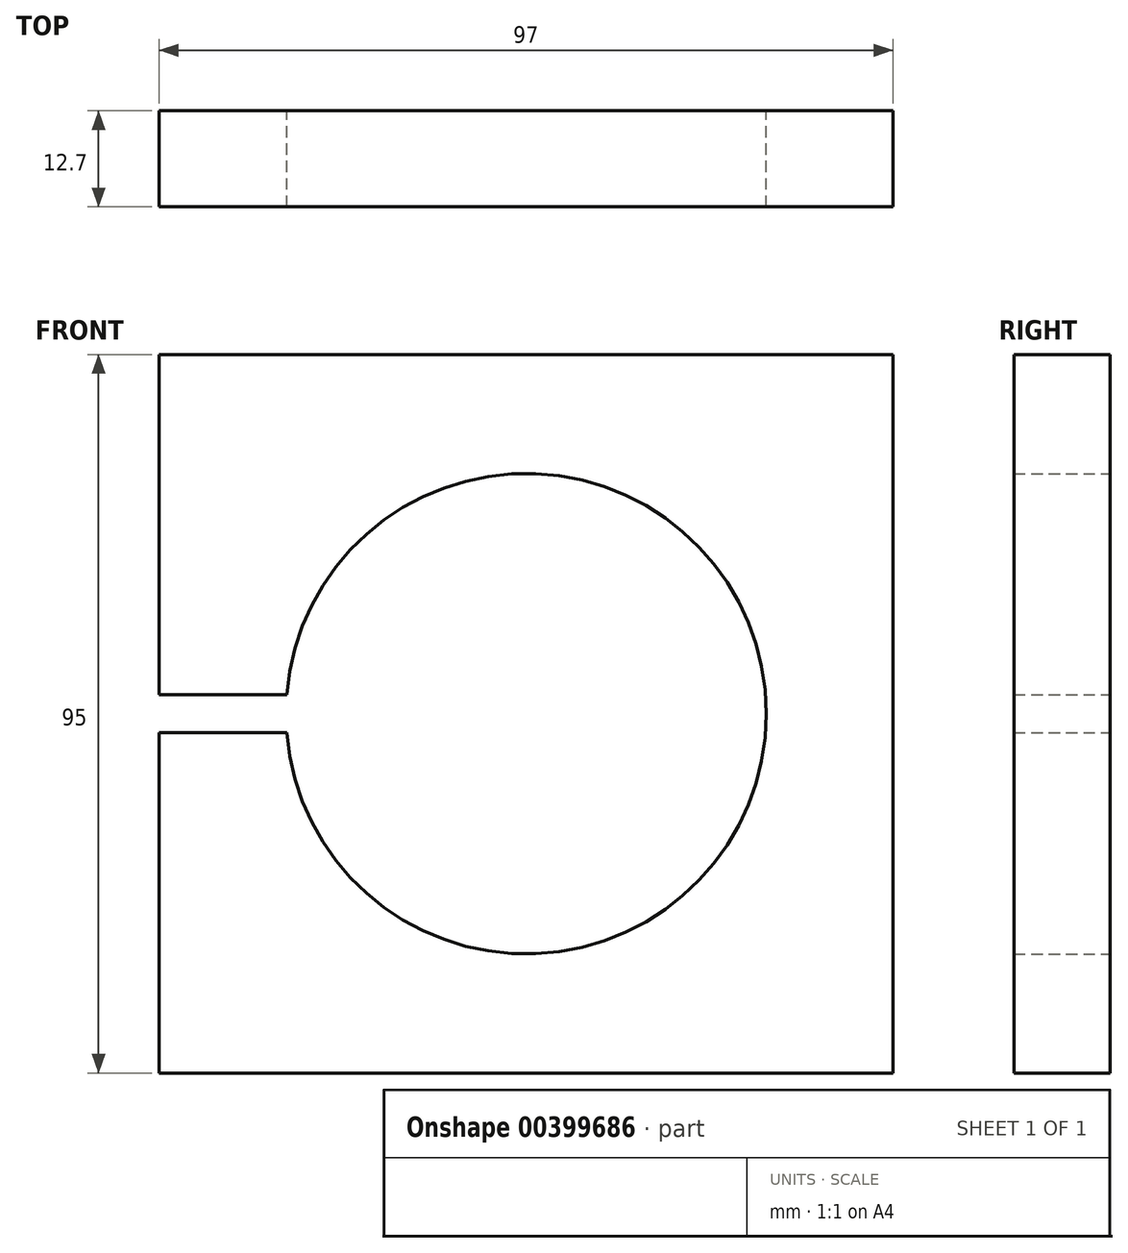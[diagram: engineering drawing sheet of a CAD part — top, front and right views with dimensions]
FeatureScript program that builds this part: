
annotation { "Feature Type Name" : "Feature", "Feature Type Description" : "" }
export const myFeature = defineFeature(function(context is Context, id is Id, definition is map)
    precondition{}
    {
        {
            var Q0;
            Q0=qCreatedBy(makeId("Front.planeOp"),FACE);
            var sketch = newSketch(context, id + "F0", { "sketchPlane" : qUnion([Q0])});
            skArc(sketch, "E0", {"start": v(-9.72, 30.23) * mm, "mid": v(-31.75, 0) * mm, "end": v(-9.72, -30.23) * mm});
            skLineSegment(sketch, "E1.bottom", {"start": v(-48.5, 47.5) * mm, "end": v(48.5, 47.5) * mm});
            skLineSegment(sketch, "E1.top", {"start": v(-48.5, -47.5) * mm, "end": v(48.5, -47.5) * mm});
            skLineSegment(sketch, "E1.left", {"start": v(-48.5, 47.5) * mm, "end": v(-48.5, -47.5) * mm});
            skLineSegment(sketch, "E1.right", {"start": v(48.5, 47.5) * mm, "end": v(48.5, -47.5) * mm});
            skLineSegment(sketch, "E2", {"start": v(0, 0) * mm, "end": v(-48.5, 0) * mm, "construction": true});
            skLineSegment(sketch, "E3", {"start": v(-48.5, 2.5) * mm, "end": v(-31.65, 2.5) * mm});
            skLineSegment(sketch, "E4.MirrorCS", {"start": v(-48.5, -2.5) * mm, "end": v(-31.65, -2.5) * mm});
            skPoint(sketch, "E5.orphan", {"position": v(-26.24, 2.5) * mm});
            skPoint(sketch, "E6.orphan", {"position": v(-26.24, -2.5) * mm});
            skLineSegment(sketch, "E7", {"start": v(-9.72, 30.23) * mm, "end": v(9.72, 30.23) * mm});
            skLineSegment(sketch, "E8.MirrorCS", {"start": v(-9.72, -30.23) * mm, "end": v(9.72, -30.23) * mm});
            skArc(sketch, "E9.trimOffspring", {"start": v(9.72, -30.23) * mm, "mid": v(31.75, 0) * mm, "end": v(9.72, 30.23) * mm});
            skCircle(sketch, "E10", {"center": v(0, 0) * mm, "radius": 31.75 * mm});
            skSolve(sketch);
        }
        {
            var Q0;
            {var subQ1=sQuery(id+"F0.wireOp",EDGE,"E1.bottom");Q0=makeQuery(id+"F0.imprint","IMPRINT",FACE,{"disambiguationData":[TD([[makeQuery(id+"F0.imprint","IMPRINT",EDGE,{"derivedFrom":subQ1}),-1.0]])]});}
            extrude(context, id + "F1", {"entities" : qUnion([Q0]), "depth" : 12.7 * mm});
        }
    });
